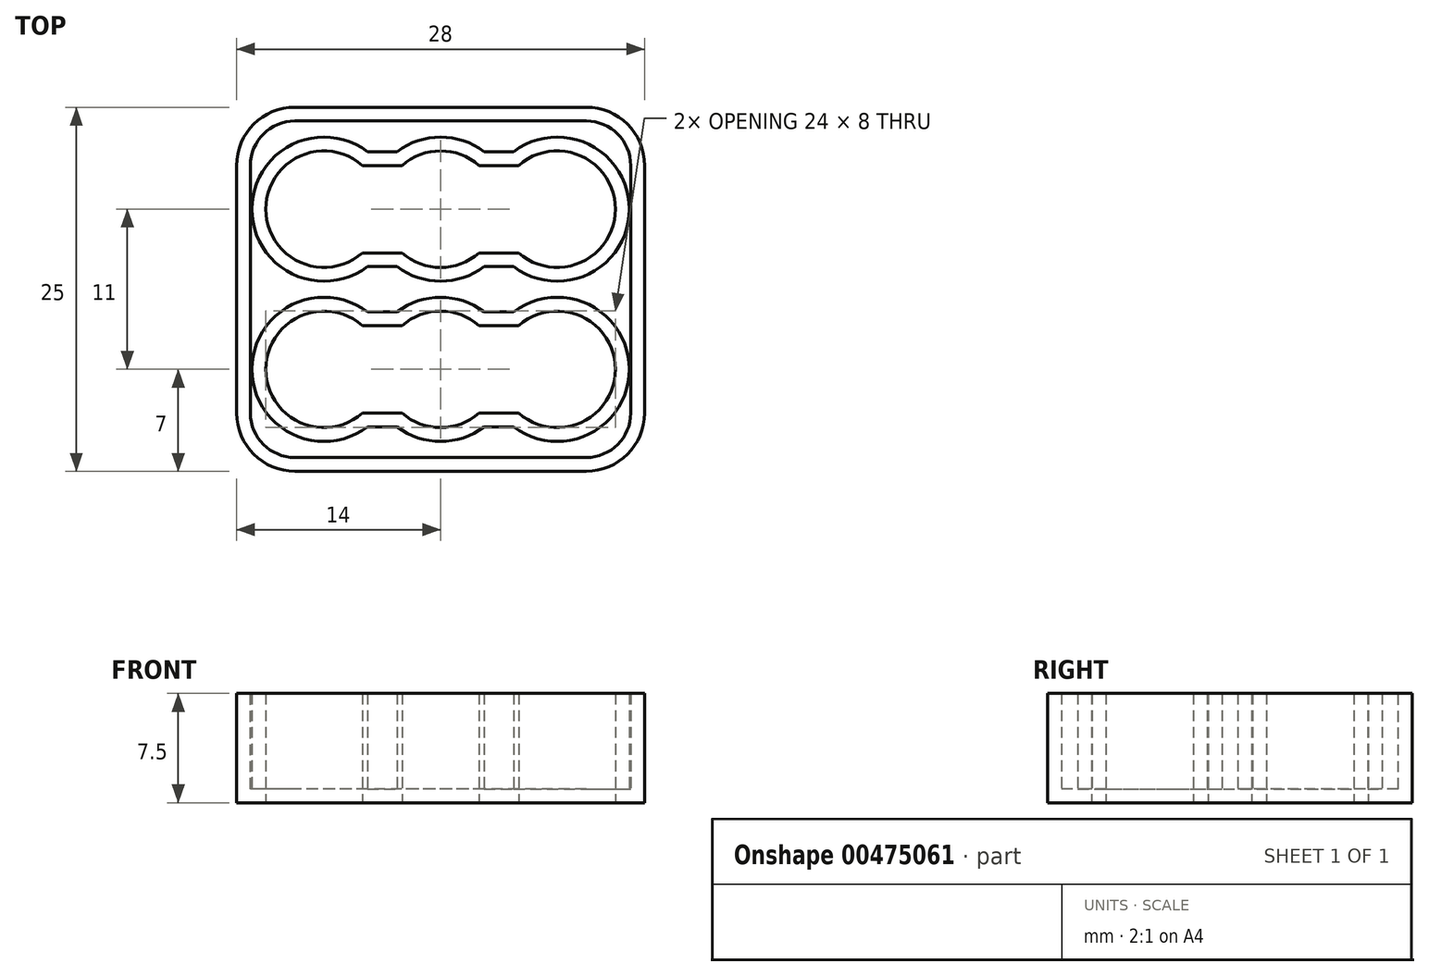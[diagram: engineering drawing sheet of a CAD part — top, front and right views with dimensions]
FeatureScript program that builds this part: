
annotation { "Feature Type Name" : "Feature", "Feature Type Description" : "" }
export const myFeature = defineFeature(function(context is Context, id is Id, definition is map)
    precondition{}
    {
        {
            var Q0;
            Q0=qCreatedBy(makeId("Top.planeOp"),FACE);
            var sketch = newSketch(context, id + "F0", { "sketchPlane" : qUnion([Q0])});
            skArc(sketch, "E0", {"start": v(-2.65, -8.6) * mm, "mid": v(0, -9.6) * mm, "end": v(2.65, -8.6) * mm});
            skArc(sketch, "E1", {"start": v(5.35, -8.6) * mm, "mid": v(8, -9.6) * mm, "end": v(10.65, -8.6) * mm});
            skArc(sketch, "E2", {"start": v(-5.35, -2.6) * mm, "mid": v(-8, -1.6) * mm, "end": v(-10.65, -2.6) * mm});
            skLineSegment(sketch, "E3", {"start": v(-18.64, -0.1) * mm, "end": v(35.35, -0.1) * mm, "construction": true});
            skArc(sketch, "E4.MirrorC", {"start": v(-5.35, 2.4) * mm, "mid": v(-12, 5.4) * mm, "end": v(-5.35, 8.4) * mm});
            skArc(sketch, "E5.MirrorC", {"start": v(2.65, 2.4) * mm, "mid": v(0, 1.4) * mm, "end": v(-2.65, 2.4) * mm});
            skArc(sketch, "E6.MirrorC", {"start": v(10.65, 2.4) * mm, "mid": v(8, 1.4) * mm, "end": v(5.35, 2.4) * mm});
            skLineSegment(sketch, "E7", {"start": v(14, -12.6) * mm, "end": v(-11.26, -12.6) * mm});
            skLineSegment(sketch, "E8", {"start": v(14, 12.4) * mm, "end": v(-14, 12.4) * mm});
            skLineSegment(sketch, "E9", {"start": v(-14, 12.4) * mm, "end": v(-14, 5.4) * mm});
            skLineSegment(sketch, "E10", {"start": v(-11.26, -12.6) * mm, "end": v(-14, -12.6) * mm});
            skLineSegment(sketch, "E11.trimOffspring", {"start": v(-2.65, 8.4) * mm, "end": v(-5.35, 8.4) * mm});
            skLineSegment(sketch, "E12.trimOffspring", {"start": v(5.35, 8.4) * mm, "end": v(2.65, 8.4) * mm});
            skArc(sketch, "E13.trimOffspring", {"start": v(5.35, 8.4) * mm, "mid": v(8, 9.4) * mm, "end": v(10.65, 8.4) * mm});
            skArc(sketch, "E14.trimOffspring", {"start": v(-2.65, 8.4) * mm, "mid": v(0, 9.4) * mm, "end": v(2.65, 8.4) * mm});
            skLineSegment(sketch, "E15", {"start": v(-5.35, -2.6) * mm, "end": v(-2.65, -2.6) * mm});
            skLineSegment(sketch, "E16", {"start": v(-5.35, -8.6) * mm, "end": v(-2.65, -8.6) * mm});
            skLineSegment(sketch, "E17.trimOffspring", {"start": v(2.65, -2.6) * mm, "end": v(5.35, -2.6) * mm});
            skLineSegment(sketch, "E18.trimOffspring", {"start": v(2.65, -8.6) * mm, "end": v(5.35, -8.6) * mm});
            skArc(sketch, "E19.trimOffspring", {"start": v(2.65, -2.6) * mm, "mid": v(0, -1.6) * mm, "end": v(-2.65, -2.6) * mm});
            skArc(sketch, "E20.trimOffspring", {"start": v(10.65, -2.6) * mm, "mid": v(8, -1.6) * mm, "end": v(5.35, -2.6) * mm});
            skArc(sketch, "E21.trimOffspring", {"start": v(-10.65, -8.6) * mm, "mid": v(-8, -9.6) * mm, "end": v(-5.35, -8.6) * mm});
            skLineSegment(sketch, "E22.trimOffspring", {"start": v(-2.65, 2.4) * mm, "end": v(-5.35, 2.4) * mm});
            skLineSegment(sketch, "E23.trimOffspring", {"start": v(5.35, 2.4) * mm, "end": v(2.65, 2.4) * mm});
            skLineSegment(sketch, "E24", {"start": v(14, 8.4) * mm, "end": v(14, 12.4) * mm});
            skLineSegment(sketch, "E25", {"start": v(14, 2.4) * mm, "end": v(14, -12.6) * mm});
            skPoint(sketch, "E26.end.orphan", {"position": v(18.26, 18) * mm});
            skPoint(sketch, "E27.end.orphan", {"position": v(22, 14) * mm});
            skPoint(sketch, "E27.start.orphan", {"position": v(22, 18) * mm});
            skPoint(sketch, "E28.center.orphan", {"position": v(16, -5.6) * mm});
            skPoint(sketch, "E29.start.orphan", {"position": v(22, 8) * mm});
            skArc(sketch, "E30", {"start": v(10.65, -8.6) * mm, "mid": v(12, -5.6) * mm, "end": v(10.65, -2.6) * mm});
            skPoint(sketch, "E31.end.orphan", {"position": v(14, -5.1) * mm});
            skPoint(sketch, "E31.start.orphan", {"position": v(12, -5.6) * mm});
            skLineSegment(sketch, "E32", {"start": v(-19.3, 5.4) * mm, "end": v(25.98, 5.4) * mm, "construction": true});
            skLineSegment(sketch, "E33", {"start": v(22.82, -5.6) * mm, "end": v(-23.22, -5.6) * mm, "construction": true});
            skArc(sketch, "E34", {"start": v(-10.65, -2.6) * mm, "mid": v(-12, -5.6) * mm, "end": v(-10.65, -8.6) * mm});
            skPoint(sketch, "E35.start.orphan", {"position": v(-14, -8.6) * mm});
            skPoint(sketch, "E36.trimOffspring.end.orphan", {"position": v(-14, -2.6) * mm});
            skLineSegment(sketch, "E37", {"start": v(-14, -12.6) * mm, "end": v(-14, 5.4) * mm});
            skLineSegment(sketch, "E38", {"start": v(14, 2.4) * mm, "end": v(14, 8.4) * mm});
            skArc(sketch, "E39", {"start": v(10.65, 2.4) * mm, "mid": v(12, 5.4) * mm, "end": v(10.65, 8.4) * mm});
            skSolve(sketch);
        }
        {
            var Q0;
            Q0=makeQuery(id+"F0.imprint","IMPRINT",FACE,{"disambiguationData":[TD([[makeQuery(id+"F0.imprint","IMPRINT",EDGE,{"derivedFrom":sQuery(id+"F0.wireOp",EDGE,"E0")}),-1.0]])]});
            extrude(context, id + "F1", {"entities" : qUnion([Q0]), "depth" : 7.5 * mm});
        }
        {
            var Q0;
            Q0=makeQuery(id+"F1.opExtrude","SWEPT_EDGE",EDGE,{"disambiguationData":[OSD([sQuery(id+"F0.wireOp",EDGE,"E8"),sQuery(id+"F0.wireOp",EDGE,"E9")])]});
            var Q1;
            Q1=makeQuery(id+"F1.opExtrude","SWEPT_EDGE",EDGE,{"disambiguationData":[OSD([sQuery(id+"F0.wireOp",EDGE,"E7"),sQuery(id+"F0.wireOp",EDGE,"E25")])]});
            var Q2;
            Q2=makeQuery(id+"F1.opExtrude","SWEPT_EDGE",EDGE,{"disambiguationData":[OSD([sQuery(id+"F0.wireOp",EDGE,"ayJ3G5tn-fuyW-xk8k-UtQO-Z51El7EXuUbb"),sQuery(id+"F0.wireOp",EDGE,"E10")])]});
            var Q3;
            Q3=makeQuery(id+"F1.opExtrude","SWEPT_EDGE",EDGE,{"disambiguationData":[OSD([sQuery(id+"F0.wireOp",EDGE,"E8"),sQuery(id+"F0.wireOp",EDGE,"E24")])]});
            fillet(context, id + "F2", {"entities" : qUnion([Q0, Q1, Q2, Q3]), "radius" : 4 * mm, "tangentPropagation" : true, "allowEdgeOverflow" : false});
        }
        {
            var Q0;
            Q0=makeQuery(id+"F1.opExtrude","CAP_FACE",FACE,{"disambiguationData":[OSD([sQuery(id+"F0.wireOp",EDGE,"E0"),sQuery(id+"F0.wireOp",EDGE,"E1"),sQuery(id+"F0.wireOp",EDGE,"E2"),sQuery(id+"F0.wireOp",EDGE,"E4.MirrorC"),sQuery(id+"F0.wireOp",EDGE,"E5.MirrorC"),sQuery(id+"F0.wireOp",EDGE,"E6.MirrorC"),sQuery(id+"F0.wireOp",EDGE,"E7"),sQuery(id+"F0.wireOp",EDGE,"E8"),sQuery(id+"F0.wireOp",EDGE,"E9"),sQuery(id+"F0.wireOp",EDGE,"E10"),sQuery(id+"F0.wireOp",EDGE,"E11.trimOffspring"),sQuery(id+"F0.wireOp",EDGE,"E12.trimOffspring"),sQuery(id+"F0.wireOp",EDGE,"E13.trimOffspring"),sQuery(id+"F0.wireOp",EDGE,"E14.trimOffspring"),sQuery(id+"F0.wireOp",EDGE,"E15"),sQuery(id+"F0.wireOp",EDGE,"E16"),sQuery(id+"F0.wireOp",EDGE,"E17.trimOffspring"),sQuery(id+"F0.wireOp",EDGE,"E18.trimOffspring"),sQuery(id+"F0.wireOp",EDGE,"E19.trimOffspring"),sQuery(id+"F0.wireOp",EDGE,"E20.trimOffspring"),sQuery(id+"F0.wireOp",EDGE,"E21.trimOffspring"),sQuery(id+"F0.wireOp",EDGE,"E22.trimOffspring"),sQuery(id+"F0.wireOp",EDGE,"E23.trimOffspring"),sQuery(id+"F0.wireOp",EDGE,"E24"),sQuery(id+"F0.wireOp",EDGE,"E25"),sQuery(id+"F0.wireOp",EDGE,"E30"),sQuery(id+"F0.wireOp",EDGE,"E34"),sQuery(id+"F0.wireOp",EDGE,"E37"),sQuery(id+"F0.wireOp",EDGE,"E38"),sQuery(id+"F0.wireOp",EDGE,"E39")])],"isStart":false});
            var Q1;
            Q1=makeQuery(id+"F1.opExtrude","SWEPT_BODY",BODY,{"disambiguationData":[OSD([sQuery(id+"F0.wireOp",EDGE,"E0"),sQuery(id+"F0.wireOp",EDGE,"E1"),sQuery(id+"F0.wireOp",EDGE,"E2"),sQuery(id+"F0.wireOp",EDGE,"E4.MirrorC"),sQuery(id+"F0.wireOp",EDGE,"E5.MirrorC"),sQuery(id+"F0.wireOp",EDGE,"E6.MirrorC"),sQuery(id+"F0.wireOp",EDGE,"E7"),sQuery(id+"F0.wireOp",EDGE,"E8"),sQuery(id+"F0.wireOp",EDGE,"E9"),sQuery(id+"F0.wireOp",EDGE,"E10"),sQuery(id+"F0.wireOp",EDGE,"E11.trimOffspring"),sQuery(id+"F0.wireOp",EDGE,"E12.trimOffspring"),sQuery(id+"F0.wireOp",EDGE,"E13.trimOffspring"),sQuery(id+"F0.wireOp",EDGE,"E14.trimOffspring"),sQuery(id+"F0.wireOp",EDGE,"E15"),sQuery(id+"F0.wireOp",EDGE,"E16"),sQuery(id+"F0.wireOp",EDGE,"E17.trimOffspring"),sQuery(id+"F0.wireOp",EDGE,"E18.trimOffspring"),sQuery(id+"F0.wireOp",EDGE,"E19.trimOffspring"),sQuery(id+"F0.wireOp",EDGE,"E20.trimOffspring"),sQuery(id+"F0.wireOp",EDGE,"E21.trimOffspring"),sQuery(id+"F0.wireOp",EDGE,"E22.trimOffspring"),sQuery(id+"F0.wireOp",EDGE,"E23.trimOffspring"),sQuery(id+"F0.wireOp",EDGE,"E24"),sQuery(id+"F0.wireOp",EDGE,"E25"),sQuery(id+"F0.wireOp",EDGE,"E30"),sQuery(id+"F0.wireOp",EDGE,"E34"),sQuery(id+"F0.wireOp",EDGE,"E37"),sQuery(id+"F0.wireOp",EDGE,"E38"),sQuery(id+"F0.wireOp",EDGE,"E39")])]});
            shell(context, id + "F3", {"entities" : qUnion([Q0]), "parts" : qUnion([Q1]), "thickness" : 0.95 * mm});
        }
    });
